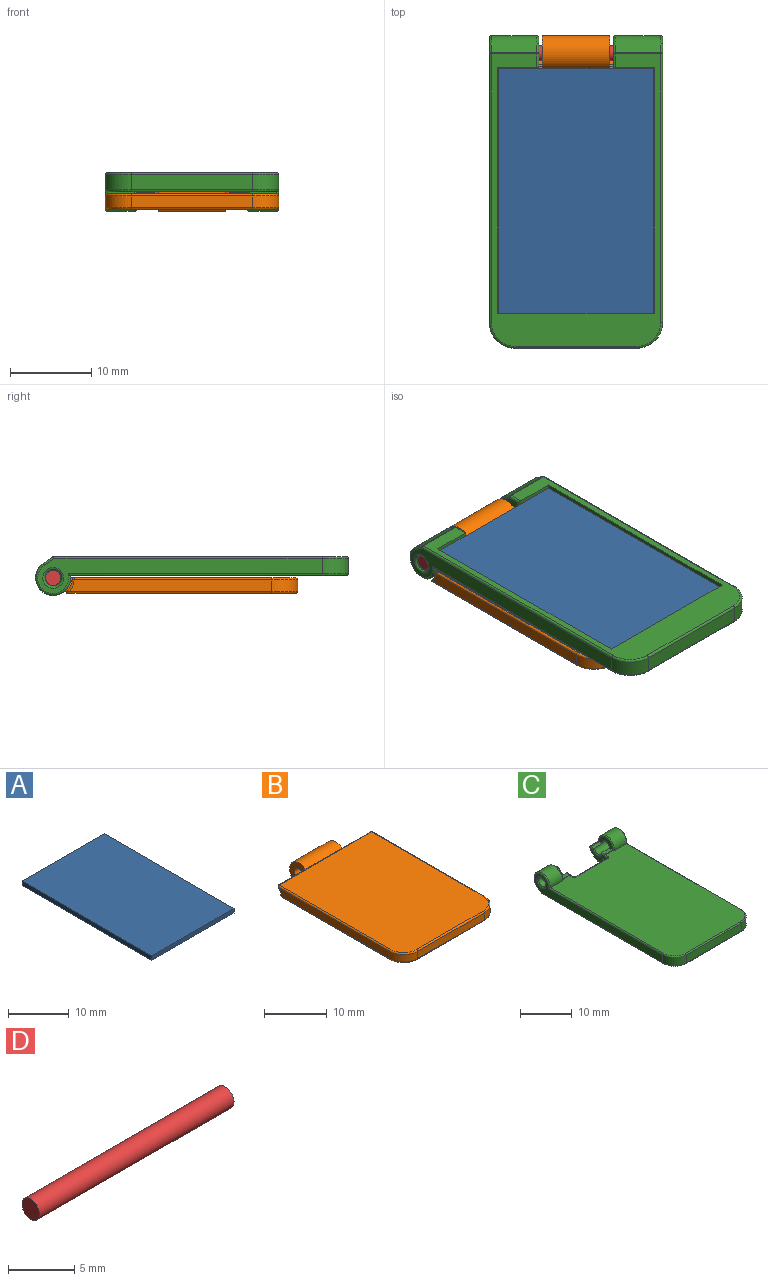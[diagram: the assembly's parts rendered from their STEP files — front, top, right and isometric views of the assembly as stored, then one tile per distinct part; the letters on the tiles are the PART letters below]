
ASSEMBLY  parts=4 mates=3
PART A: 6 faces, bbox 19.1x30.1x0.9 mm
  f0: plane 30.12x0.9mm, normal (-1,0,0), area 27.1mm2, adj f1,f3,f4,f5
  f1: plane 19.05x0.9mm, normal (0,-1,0), area 17.1mm2, adj f0,f2,f4,f5
  f2: plane 30.12x0.9mm, normal (1,0,0), area 27.1mm2, adj f1,f3,f4,f5
  f3: plane 19.05x0.9mm, normal (0,1,0), area 17.1mm2, adj f0,f2,f4,f5
  f4: plane 30.12x19.05mm, normal (0,0,1), area 573.9mm2, adj f0,f1,f2,f3
  f5: plane 30.12x19.05mm, normal (0,0,-1), area 573.9mm2, adj f0,f1,f2,f3
PART B: 49 faces, bbox 21.9x32.5x4.3 mm
  f0: plane 28.04x20.84mm, normal (0,0,1), area 580.7mm2, adj f35,f38,f39,f46,f47,f48
  f1: plane 24.95x1.41mm, normal (1,0,0), area 34.5mm2, adj f24,f32,f39,f42
  f2: cylinder r=2.34mm len=3.89mm, axis (1,0,0), area 5.9mm2, adj f11,f16,f20,f26,f29,f30
  f3: cylinder r=2.34mm len=3.88mm, axis (1,0,0), area 5.9mm2, adj f12,f23,f27,f31,f32
  f4: plane 28.19x20.84mm, normal (0,0,-1), area 572.7mm2, adj f8,f9,f12,f13,f15,f16,f18,f19
  f5: plane 12.58x0.75mm, normal (0,0.74,0.67), area 6.8mm2, adj f6,f7,f8,f9,f13,f26,f27,f35
  f6: cylinder r=1.44mm len=2.16mm, axis (-1,0,0), area 2.2mm2, adj f5,f9,f15,f21
  f7: cylinder r=1.44mm len=2.16mm, axis (-1,0,0), area 2.2mm2, adj f5,f8,f18,f22
  f8: plane 4.3x4.3mm, normal (1,0,0), area 10.2mm2, adj f4,f5,f7,f10,f13,f18
  f9: plane 4.3x4.3mm, normal (-1,0,0), area 10.2mm2, adj f4,f5,f6,f10,f13,f15
  f10: cylinder r=1.02mm len=8.26mm, axis (-1,0,0), area 52.7mm2, adj f8,f9
  f11: plane 1.31x1.02mm, normal (-1,0,0), area 0.8mm2, adj f2,f16,f21,f26
  f12: plane 1.56x1.27mm, normal (1,0,0), area 0.9mm2, adj f3,f4,f22,f23,f27
  f13: cylinder r=2.15mm len=8.26mm, axis (-1,0,0), area 96.6mm2, adj f4,f5,f8,f9
  f14: plane 24.95x1.41mm, normal (-1,0,0), area 34.5mm2, adj f19,f29,f38,f41
  f15: cylinder r=0.25mm len=2.16mm, axis (-1,0,0), area 0.8mm2, adj f4,f6,f9,f17
  f16: cylinder r=0.25mm len=0.9mm, axis (0,1,0), area 0.3mm2, adj f2,f4,f11,f17,f20
  f17: sphere r=0.25mm, area 0.1mm2, adj f15,f16,f21
  f18: cylinder r=0.25mm len=2.41mm, axis (-1,0,0), area 0.8mm2, adj f4,f7,f8,f22
  f19: cylinder r=0.25mm len=24.36mm, axis (0,1,0), area 9.6mm2, adj f4,f14,f25,f43
  f20: cylinder r=0.25mm len=4.14mm, axis (1,0,0), area 1.5mm2, adj f2,f4,f16,f25
  f21: torus R=1.69mm, axis (-1,0,0), area 0.4mm2, adj f6,f11,f17,f26
  f22: torus R=1.69mm, axis (1,0,0), area 0.4mm2, adj f4,f7,f12,f18,f27
  f23: cylinder r=0.25mm len=3.88mm, axis (1,0,0), area 1.4mm2, adj f3,f4,f12,f28
  f24: cylinder r=0.25mm len=24.36mm, axis (0,-1,0), area 9.6mm2, adj f1,f4,f28,f45
  f25: sphere r=0.25mm, area 0.1mm2, adj f19,f20,f29
  f26: cylinder r=0.25mm len=0.96mm, axis (0,0.67,-0.74), area 0.3mm2, adj f2,f5,f11,f21,f30,f35
  f27: cylinder r=0.25mm len=0.96mm, axis (0,-0.67,0.74), area 0.3mm2, adj f3,f5,f12,f22,f31,f35
  f28: sphere r=0.25mm, area 0.1mm2, adj f23,f24,f32
  f29: torus R=2.59mm, axis (-1,0,0), area 0.6mm2, adj f2,f14,f25,f33,f38
  f30: cylinder r=0.25mm len=4.08mm, axis (1,0,0), area 1.2mm2, adj f2,f26,f33,f35
  f31: cylinder r=0.25mm len=4.06mm, axis (1,0,0), area 1.2mm2, adj f3,f27,f34,f35
  f32: torus R=2.59mm, axis (1,0,0), area 0.6mm2, adj f1,f3,f28,f34,f39
  f33: sphere r=0.25mm, area 0.1mm2, adj f29,f30,f36,f38
  f34: sphere r=0.25mm, area 0.1mm2, adj f31,f32,f37,f39
  f35: cylinder r=0.25mm len=20.84mm, axis (1,0,0), area 3.8mm2, adj f0,f5,f26,f27,f30,f31,f36,f37
  f36: sphere r=0.25mm, area 0mm2, adj f33,f35,f38
  f37: sphere r=0.25mm, area 0mm2, adj f34,f35,f39
  f38: cylinder r=0.25mm len=25.11mm, axis (0,1,0), area 9.9mm2, adj f0,f14,f29,f33,f36,f48
  f39: cylinder r=0.25mm len=25.11mm, axis (0,-1,0), area 9.9mm2, adj f0,f1,f32,f34,f37,f46
  f40: plane 14.99x1.41mm, normal (0,-1,0), area 21.1mm2, adj f41,f42,f44,f47
  f41: cylinder r=3.17mm len=3.18mm, axis (0,0,1), area 7mm2, adj f14,f40,f43,f48
  f42: cylinder r=3.17mm len=3.18mm, axis (0,0,1), area 7mm2, adj f1,f40,f45,f46
  f43: torus R=2.93mm, axis (0,0,1), area 1.9mm2, adj f4,f19,f41,f44
  f44: cylinder r=0.25mm len=14.99mm, axis (1,0,0), area 5.9mm2, adj f4,f40,f43,f45
  f45: torus R=2.93mm, axis (0,0,1), area 1.9mm2, adj f4,f24,f42,f44
  f46: torus R=2.93mm, axis (0,0,1), area 1.9mm2, adj f0,f39,f42,f47
  f47: cylinder r=0.25mm len=14.99mm, axis (1,0,0), area 5.9mm2, adj f0,f40,f46,f48
  f48: torus R=2.93mm, axis (0,0,1), area 1.9mm2, adj f0,f38,f41,f47
PART C: 87 faces, bbox 22x39.1x5.1 mm
  f0: plane 34.28x20.92mm, normal (0,0,1), area 695.6mm2, adj f21,f22,f24,f25,f43,f46,f47,f48
  f1: plane 19.3x1.27mm, normal (0,1,0), area 24.5mm2, adj f3,f23,f28,f29
  f2: plane 4.83x1.27mm, normal (0,-1,0), area 6.1mm2, adj f3,f23,f28,f49
  f3: plane 30.38x19.46mm, normal (0,0,-1), area 572.6mm2, adj f1,f2,f26,f28,f29,f53,f54,f56
  f4: plane 35.06x4.28mm, normal (1,0,0), area 66.7mm2, adj f31,f64,f69,f74,f75,f85
  f5: plane 35.06x4.28mm, normal (-1,0,0), area 66.7mm2, adj f30,f63,f65,f79,f80,f86
  f6: plane 4.45x2.03mm, normal (1,0,0), area 4.4mm2, adj f32,f34,f35,f38,f41,f43,f44,f49
  f7: plane 2.04x0.07mm, normal (0,0,1), area 0.1mm2, adj f9,f17,f24,f40
  f8: cylinder r=2.88mm len=8.64mm, axis (1,0,0), area 5mm2, adj f47,f52,f55,f58
  f9: plane 3.8x2.06mm, normal (-1,0,0), area 4.2mm2, adj f7,f15,f16,f17,f20,f24,f59
  f10: plane 3.8x2.06mm, normal (1,0,0), area 3.3mm2, adj f11,f12,f13,f14,f25,f60,f61
  f11: plane 1.28x0.06mm, normal (0,0,1), area 0mm2, adj f10,f14,f25
  f12: plane 2.53x0.47mm, normal (0,0.05,1), area 0.7mm2, adj f10,f13,f21,f32,f35,f60
  f13: plane 2.29x0.82mm, normal (0,-0.01,1), area 1.7mm2, adj f10,f12,f19,f32,f61
  f14: plane 2.29x0.89mm, normal (0,-0.01,1), area 1.8mm2, adj f10,f11,f19,f25,f38,f61
  f15: plane 2.53x0.47mm, normal (0,0.05,1), area 0.7mm2, adj f9,f16,f22,f33,f36,f59
  f16: plane 2.04x0.81mm, normal (0,-0.01,1), area 1.7mm2, adj f9,f15,f20,f33
  f17: plane 2.04x0.82mm, normal (0,-0.01,1), area 1.7mm2, adj f7,f9,f20,f40
  f18: plane 4.45x2.03mm, normal (-1,0,0), area 4.4mm2, adj f33,f36,f37,f39,f40,f42,f45,f46
  f19: cylinder r=1.02mm len=5.6mm, axis (-1,0,0), area 27.9mm2, adj f13,f14,f34,f61,f86
  f20: cylinder r=1.02mm len=5.6mm, axis (-1,0,0), area 28.8mm2, adj f9,f16,f17,f37,f85
  f21: cylinder r=2.15mm len=5.6mm, axis (-1,0,0), area 34.5mm2, adj f0,f12,f35,f60,f73,f79
  f22: cylinder r=2.15mm len=5.6mm, axis (1,0,0), area 34.5mm2, adj f0,f15,f27,f36,f59,f74
  f23: plane 35.99x20.84mm, normal (0,0,-1), area 146.3mm2, adj f1,f2,f26,f28,f29,f30,f31,f44
  f24: plane 2.04x0.13mm, normal (0,-1,0), area 0.3mm2, adj f0,f7,f9,f42,f59
  f25: plane 2.04x0.13mm, normal (0,-1,0), area 0.3mm2, adj f0,f10,f11,f14,f41,f60
  f26: plane 4.83x1.27mm, normal (0,-1,0), area 6.1mm2, adj f3,f23,f29,f50
  f27: plane 5.6x1.18mm, normal (0,0.57,-0.82), area 8mm2, adj f22,f39,f75,f77
  f28: plane 30.23x1.27mm, normal (1,0,0), area 38.4mm2, adj f1,f2,f3,f23
  f29: plane 30.23x1.27mm, normal (-1,0,0), area 38.4mm2, adj f1,f3,f23,f26
  f30: cylinder r=0.25mm len=33.06mm, axis (0,1,0), area 13mm2, adj f5,f23,f72,f82
  f31: cylinder r=0.25mm len=33.06mm, axis (0,-1,0), area 13mm2, adj f4,f23,f70,f76
  f32: cylinder r=0.25mm len=1.12mm, axis (0,-1,-0.01), area 0.3mm2, adj f6,f12,f13,f34,f35
  f33: cylinder r=0.25mm len=1.12mm, axis (0,1,0.01), area 0.3mm2, adj f15,f16,f18,f36,f37
  f34: torus R=1.27mm, axis (1,0,0), area 1.2mm2, adj f6,f19,f32,f38
  f35: torus R=1.9mm, axis (1,0,0), area 0.7mm2, adj f6,f12,f21,f32,f81
  f36: torus R=1.9mm, axis (-1,0,0), area 0.7mm2, adj f15,f18,f22,f33,f39
  f37: torus R=1.27mm, axis (-1,0,0), area 1.2mm2, adj f18,f20,f33,f40
  f38: cylinder r=0.25mm len=0.89mm, axis (0,-1,-0.01), area 0.3mm2, adj f6,f14,f34,f41
  f39: cylinder r=0.25mm len=1.32mm, axis (0,-0.82,-0.57), area 0.6mm2, adj f18,f27,f36,f78
  f40: cylinder r=0.25mm len=0.89mm, axis (0,1,0.01), area 0.3mm2, adj f7,f17,f18,f37,f42
  f41: cylinder r=0.25mm len=0.38mm, axis (0,0,-1), area 0.1mm2, adj f6,f25,f38,f43
  f42: cylinder r=0.25mm len=0.38mm, axis (0,0,1), area 0.1mm2, adj f18,f24,f40,f46
  f43: cylinder r=0.25mm len=0.94mm, axis (0,-1,0), area 0.3mm2, adj f0,f6,f41,f48
  f44: cylinder r=0.25mm len=1.69mm, axis (0,1,0), area 0.6mm2, adj f6,f23,f49,f83
  f45: cylinder r=0.25mm len=1.69mm, axis (0,-1,0), area 0.6mm2, adj f18,f23,f50,f78
  f46: cylinder r=0.25mm len=0.94mm, axis (0,1,0), area 0.3mm2, adj f0,f18,f42,f51
  f47: cylinder r=0.25mm len=8.64mm, axis (1,0,0), area 3mm2, adj f0,f8,f48,f51
  f48: bspline ~0.58x0.56mm, area 0.2mm2, adj f0,f43,f47,f52
  f49: cylinder r=0.25mm len=1.52mm, axis (0,0,1), area 0.5mm2, adj f2,f6,f44,f53
  f50: cylinder r=0.25mm len=1.52mm, axis (0,0,1), area 0.5mm2, adj f18,f26,f45,f54
  f51: bspline ~0.59x0.57mm, area 0.2mm2, adj f0,f46,f47,f55
  f52: torus R=2.63mm, axis (1,0,0), area 0.2mm2, adj f6,f8,f48,f56
  f53: cylinder r=0.25mm len=0.85mm, axis (0,-1,0), area 0.3mm2, adj f3,f6,f49,f56
  f54: cylinder r=0.25mm len=0.85mm, axis (0,1,0), area 0.3mm2, adj f3,f18,f50,f57
  f55: torus R=2.63mm, axis (-1,0,0), area 0.2mm2, adj f8,f18,f51,f57
  f56: bspline ~0.66x0.57mm, area 0.3mm2, adj f3,f52,f53,f58
  f57: bspline ~0.71x0.53mm, area 0.3mm2, adj f3,f54,f55,f58
  f58: cylinder r=0.25mm len=8.64mm, axis (1,0,0), area 4.2mm2, adj f3,f8,f56,f57
  f59: torus R=1.9mm, axis (-1,0,0), area 2.7mm2, adj f0,f9,f15,f22,f24
  f60: torus R=1.9mm, axis (1,0,0), area 2.7mm2, adj f0,f10,f12,f21,f25
  f61: torus R=1.27mm, axis (1,0,0), area 1.5mm2, adj f10,f13,f14,f19
  f62: plane 14.99x1.88mm, normal (0,-1,0), area 28.1mm2, adj f63,f64,f67,f71
  f63: cylinder r=3.17mm len=3.18mm, axis (0,0,1), area 9.4mm2, adj f5,f62,f66,f72
  f64: cylinder r=3.17mm len=3.18mm, axis (0,0,1), area 9.4mm2, adj f4,f62,f68,f70
  f65: cylinder r=0.25mm len=31.33mm, axis (0,1,0), area 12.2mm2, adj f0,f5,f66,f79
  f66: torus R=2.93mm, axis (0,0,1), area 1.9mm2, adj f0,f63,f65,f67
  f67: cylinder r=0.25mm len=14.99mm, axis (-1,0,0), area 5.9mm2, adj f0,f62,f66,f68
  f68: torus R=2.93mm, axis (0,0,1), area 1.9mm2, adj f0,f64,f67,f69
  f69: cylinder r=0.25mm len=31.33mm, axis (0,-1,0), area 12.2mm2, adj f0,f4,f68,f74
  f70: torus R=2.93mm, axis (0,0,1), area 1.9mm2, adj f23,f31,f64,f71
  f71: cylinder r=0.25mm len=14.99mm, axis (1,0,0), area 5.9mm2, adj f23,f62,f70,f72
  f72: torus R=2.93mm, axis (0,0,1), area 1.9mm2, adj f23,f30,f63,f71
  f73: plane 5.6x1.18mm, normal (0,0.57,-0.82), area 8mm2, adj f21,f80,f81,f84
  f74: torus R=1.9mm, axis (1,0,0), area 3.5mm2, adj f4,f22,f69,f75
  f75: cylinder r=0.25mm len=1.32mm, axis (0,0.82,0.57), area 0.6mm2, adj f4,f27,f74,f76
  f76: sphere r=0.25mm, area 0mm2, adj f31,f75,f77
  f77: cylinder r=0.25mm len=5.6mm, axis (-1,0,0), area 0.8mm2, adj f23,f27,f76,f78
  f78: sphere r=0.25mm, area 0.1mm2, adj f39,f45,f77
  f79: torus R=1.9mm, axis (-1,0,0), area 3.5mm2, adj f5,f21,f65,f80
  f80: cylinder r=0.25mm len=1.32mm, axis (0,-0.82,-0.57), area 0.6mm2, adj f5,f73,f79,f82
  f81: cylinder r=0.25mm len=1.32mm, axis (0,0.82,0.57), area 0.6mm2, adj f6,f35,f73,f83
  f82: sphere r=0.25mm, area 0.1mm2, adj f30,f80,f84
  f83: sphere r=0.25mm, area 0mm2, adj f44,f81,f84
  f84: cylinder r=0.25mm len=5.6mm, axis (1,0,0), area 0.8mm2, adj f23,f73,f82,f83
  f85: torus R=1.27mm, axis (1,0,0), area 2.7mm2, adj f4,f20
  f86: torus R=1.27mm, axis (-1,0,0), area 2.7mm2, adj f5,f19
PART D: 3 faces, bbox 20.8x1.9x1.9 mm
  f0: cylinder r=0.94mm len=20.83mm, axis (-1,0,0), area 123mm2, adj f1,f2
  f1: plane 1.88x1.88mm, normal (1,0,0), area 2.8mm2, adj f0
  f2: plane 1.88x1.88mm, normal (-1,0,0), area 2.8mm2, adj f0
PLACE A rot(axis=(-1,0,0),0deg) t=(0.87,-0.84,1.73)mm
PLACE B rot(axis=(0,1,0),180deg) t=(0.87,4.22,-1.21)mm fixed
PLACE C rot(axis=(0,1,0),180deg) t=(0.87,4.22,-1.21)mm
PLACE D rot(axis=(0,1,0),180deg) t=(7.22,13.75,0.37)mm
MATE fastened D.f0 <-> B.f2  axis (1,0,0) through (0.87,13.75,0.37)mm
MATE fastened A.f1 <-> C.f1  axis (0,-1,0) through (0.87,-18.27,1.73)mm
MATE revolute C.f8 <-> D.f0  axis (1,0,0) through (11.28,13.75,0.37)mm
